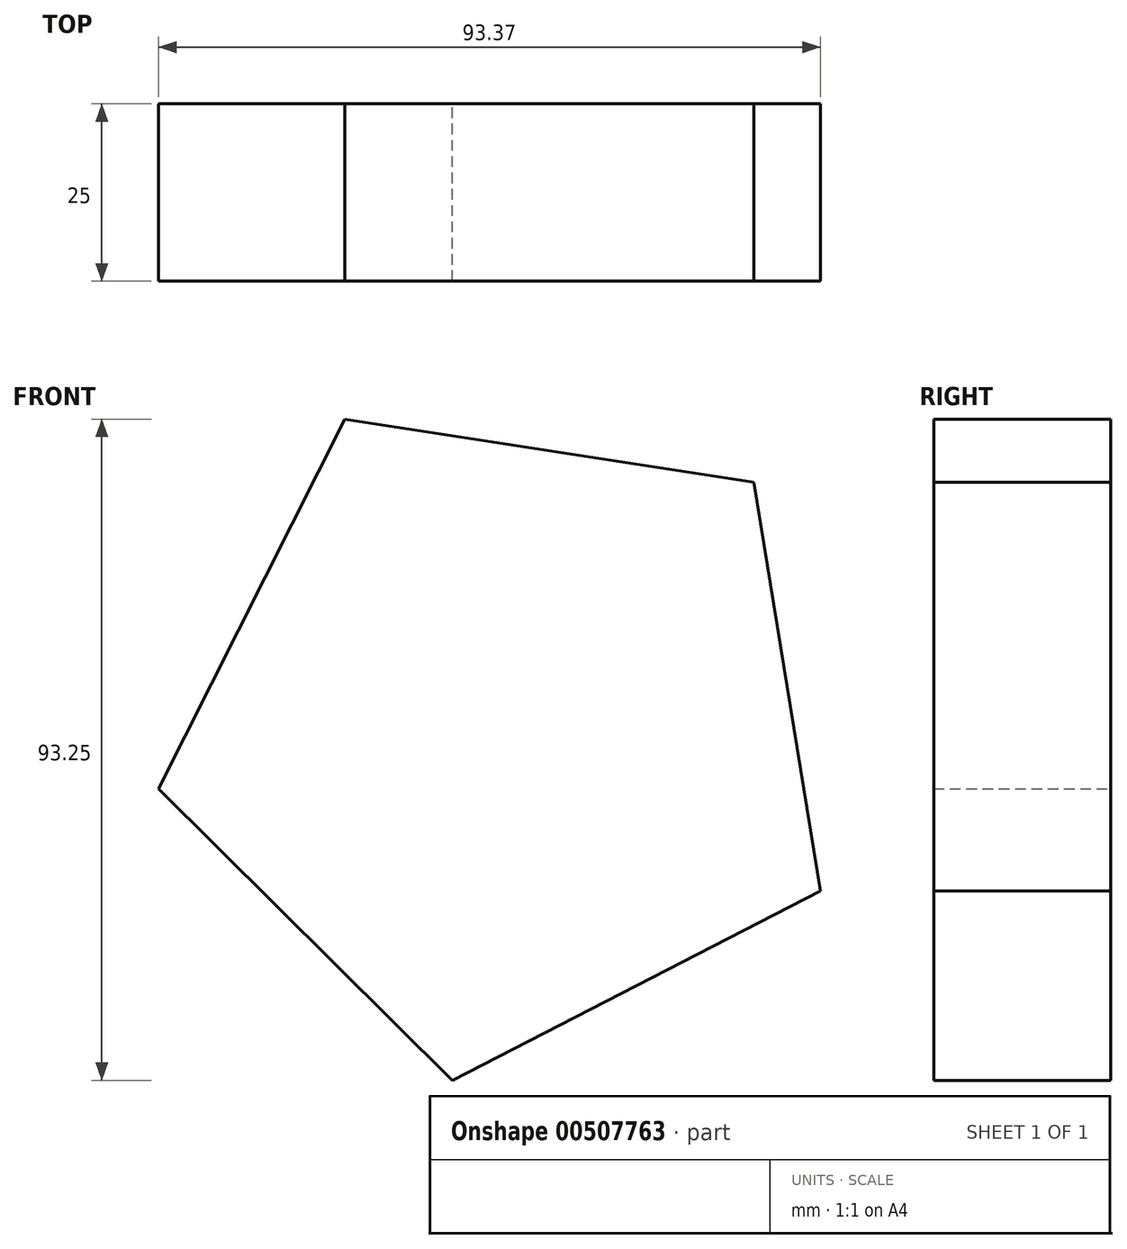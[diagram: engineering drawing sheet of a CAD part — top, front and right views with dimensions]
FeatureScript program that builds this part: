
annotation { "Feature Type Name" : "Feature", "Feature Type Description" : "" }
export const myFeature = defineFeature(function(context is Context, id is Id, definition is map)
    precondition{}
    {
        {
            var Q0;
            Q0=qCreatedBy(makeId("Front.planeOp"),FACE);
            var sketch = newSketch(context, id + "F0", { "sketchPlane" : qUnion([Q0])});
            skCircle(sketch, "E0.cCircle", {"center": v(0, 0) * mm, "radius": 49.67 * mm, "construction": true});
            skLineSegment(sketch, "E0.0", {"start": v(-22.74, 44.16) * mm, "end": v(34.97, 35.27) * mm});
            skLineSegment(sketch, "E0.1", {"start": v(34.97, 35.27) * mm, "end": v(44.35, -22.36) * mm});
            skLineSegment(sketch, "E0.2", {"start": v(44.35, -22.36) * mm, "end": v(-7.56, -49.09) * mm});
            skLineSegment(sketch, "E0.3", {"start": v(-7.56, -49.09) * mm, "end": v(-49.02, -7.98) * mm});
            skLineSegment(sketch, "E0.4", {"start": v(-49.02, -7.98) * mm, "end": v(-22.74, 44.16) * mm});
            skSolve(sketch);
        }
        {
            var Q0;
            Q0=makeQuery(id+"F0.imprint","IMPRINT",FACE,{"disambiguationData":[TD([[makeQuery(id+"F0.imprint","IMPRINT",EDGE,{"derivedFrom":sQuery(id+"F0.wireOp",EDGE,"E0.0")}),-1.0]])]});
            extrude(context, id + "F1", {"entities" : qUnion([Q0]), "depth" : 25 * mm});
        }
    });
